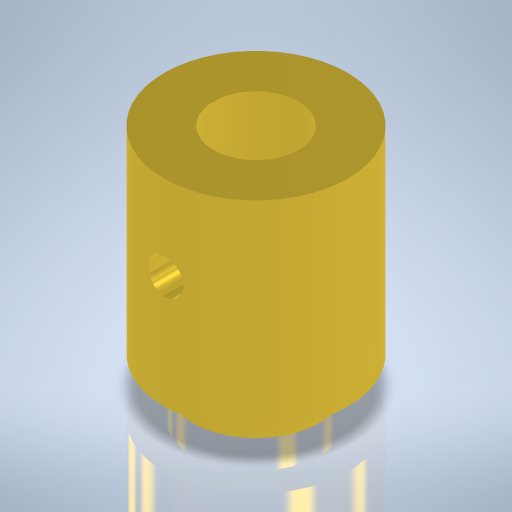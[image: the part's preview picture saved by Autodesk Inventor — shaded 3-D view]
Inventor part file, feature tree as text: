
AUTODESK INVENTOR PART (.ipt)
format: ipt  version: 2024 (Build 280153000, 153)  size: 251,904 bytes
history: native  units: mm
features: sketch x4, hole x2, revolve x1, plane x1, extrude x1
ambient origin geometry x8: Origin, YZ Plane, XZ Plane, XY Plane, X Axis, Y Axis, Z Axis, Center Point
bodies: Volumenkörper1 (feature_tree)
feature tree (9):
  revolve  "Umdrehung1"
  plane  "Arbeitsebene1"
  hole  "Bohrung2"  [1 undecoded]
  extrude  "Extrusion1"  Depth=6.5mm
  hole  "Bohrung3"  [1 undecoded]
  sketch  "Skizze1"  dims[d0=13.0mm d1=14.0mm]
  sketch  "Skizze3"  dims[d2=90.0deg d10=6.5mm]
  sketch  "Skizze4"  dims[d11=6.0mm]
  sketch  "Skizze6"  dims[d12=2.5mm d13=6.0mm d14=4.0mm d15=2.0mm d16=90.0deg d17=8.0mm d18=0.0mm d19=6.0mm d20=6.0mm d21=4.0mm d22=2.0mm d23=90.0deg d24=6.0mm d25=0.0mm d33=2.0mm d34=0.0mm]
note: 2 required parameter values undecoded (feature->parameter linkage not recoverable at this tier; creation-order binding heuristic only, values carry confidence <= 0.55)
